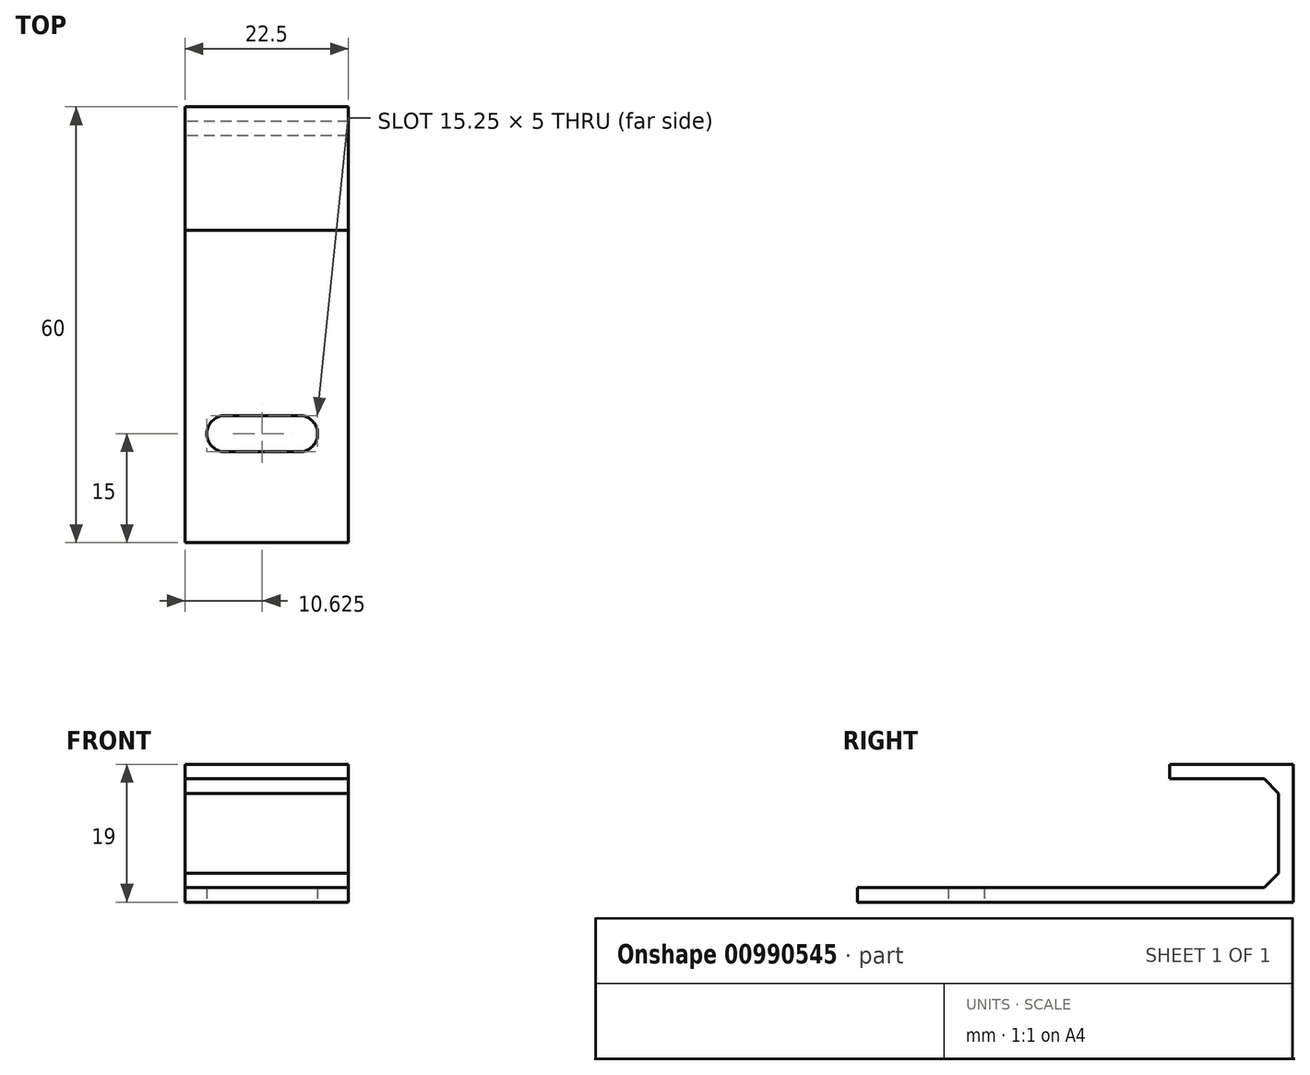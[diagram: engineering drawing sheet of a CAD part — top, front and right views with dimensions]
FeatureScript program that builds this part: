
annotation { "Feature Type Name" : "Feature", "Feature Type Description" : "" }
export const myFeature = defineFeature(function(context is Context, id is Id, definition is map)
    precondition{}
    {
        {
            assignVariable(context, id + "F0", {"name" : "noz", "anyValue" : .5});
        }
        {
            assignVariable(context, id + "F1", {"name" : "shells", "anyValue" : 4});
        }
        {
            assignVariable(context, id + "F2", {"name" : "wall", "anyValue" : getVariable(context, 'noz') * getVariable(context, 'shells')});
        }
        {
            assignVariable(context, id + "F3", {"name" : "hole", "anyValue" : 4.5});
        }
        {
            var Q0;
            Q0=qCreatedBy(makeId("Top.planeOp"),FACE);
            var sketch = newSketch(context, id + "F4", { "sketchPlane" : qUnion([Q0])});
            skLineSegment(sketch, "E0.bottom", {"start": v(21.25, 40.92) * mm, "end": v(-21.25, 40.92) * mm, "construction": true});
            skLineSegment(sketch, "E0.top", {"start": v(21.25, -40.93) * mm, "end": v(-21.25, -40.93) * mm, "construction": true});
            skLineSegment(sketch, "E0.left", {"start": v(21.25, 40.93) * mm, "end": v(21.25, -40.93) * mm, "construction": true});
            skLineSegment(sketch, "E0.right", {"start": v(-21.25, 40.93) * mm, "end": v(-21.25, -40.93) * mm, "construction": true});
            skPoint(sketch, "E0.middle", {"position": v(0, 0) * mm});
            skLineSegment(sketch, "E1.bottom", {"start": v(48, 75.25) * mm, "end": v(-48, 75.25) * mm, "construction": true});
            skLineSegment(sketch, "E1.top", {"start": v(48, -75.25) * mm, "end": v(-48, -75.25) * mm, "construction": true});
            skLineSegment(sketch, "E1.left", {"start": v(48, 75.25) * mm, "end": v(48, -75.25) * mm});
            skLineSegment(sketch, "E1.right", {"start": v(-48, 75.25) * mm, "end": v(-48, -75.25) * mm});
            skLineSegment(sketch, "E2.bottom", {"start": v(-6.25, 40.92) * mm, "end": v(6.25, 40.92) * mm, "construction": true});
            skLineSegment(sketch, "E2.top", {"start": v(-6.25, 45.92) * mm, "end": v(6.25, 45.92) * mm, "construction": true});
            skLineSegment(sketch, "E2.left", {"start": v(-6.25, 40.92) * mm, "end": v(-6.25, 45.92) * mm, "construction": true});
            skLineSegment(sketch, "E2.right", {"start": v(6.25, 40.92) * mm, "end": v(6.25, 45.92) * mm, "construction": true});
            skLineSegment(sketch, "E3.bottom", {"start": v(-21.25, 40.92) * mm, "end": v(-6.25, 40.92) * mm, "construction": true});
            skLineSegment(sketch, "E3.top", {"start": v(-21.25, 75.25) * mm, "end": v(-6.25, 75.25) * mm, "construction": true});
            skLineSegment(sketch, "E3.left", {"start": v(-21.25, 40.92) * mm, "end": v(-21.25, 75.25) * mm, "construction": true});
            skLineSegment(sketch, "E3.right", {"start": v(-6.25, 40.92) * mm, "end": v(-6.25, 75.25) * mm, "construction": true});
            skLineSegment(sketch, "E4.bottom", {"start": v(6.25, 40.92) * mm, "end": v(21.25, 40.92) * mm, "construction": true});
            skLineSegment(sketch, "E4.top", {"start": v(6.25, 75.25) * mm, "end": v(21.25, 75.25) * mm, "construction": true});
            skLineSegment(sketch, "E4.left", {"start": v(6.25, 40.92) * mm, "end": v(6.25, 75.25) * mm, "construction": true});
            skLineSegment(sketch, "E4.right", {"start": v(21.25, 40.92) * mm, "end": v(21.25, 75.25) * mm, "construction": true});
            skLineSegment(sketch, "E5", {"start": v(0, 91.05) * mm, "end": v(0, -104.71) * mm, "construction": true});
            skCircle(sketch, "E6", {"center": v(-43, 60.25) * mm, "radius": 2.5 * mm});
            skCircle(sketch, "E7.MirrorC", {"center": v(43, 60.25) * mm, "radius": 2.5 * mm});
            skLineSegment(sketch, "E8.bottom", {"start": v(-48, -75.25) * mm, "end": v(48, -75.25) * mm, "construction": true});
            skLineSegment(sketch, "E8.top", {"start": v(-48, -88.75) * mm, "end": v(48, -88.75) * mm, "construction": true});
            skLineSegment(sketch, "E8.left", {"start": v(-48, -75.25) * mm, "end": v(-48, -88.75) * mm, "construction": true});
            skLineSegment(sketch, "E8.right", {"start": v(48, -75.25) * mm, "end": v(48, -88.75) * mm, "construction": true});
            skCircle(sketch, "E9", {"center": v(0, -82) * mm, "radius": 2.5 * mm, "construction": true});
            skLineSegment(sketch, "E10.bottom", {"start": v(-48, 45.25) * mm, "end": v(48, 45.25) * mm});
            skLineSegment(sketch, "E10.top", {"start": v(-48, 105.25) * mm, "end": v(48, 105.25) * mm});
            skLineSegment(sketch, "E10.left", {"start": v(-48, 45.25) * mm, "end": v(-48, 105.25) * mm});
            skLineSegment(sketch, "E10.right", {"start": v(48, 45.25) * mm, "end": v(48, 105.25) * mm});
            skLineSegment(sketch, "E11", {"start": v(-48, 85.25) * mm, "end": v(48, 85.25) * mm});
            skLineSegment(sketch, "E12", {"start": v(-48, 103.25) * mm, "end": v(48, 103.25) * mm});
            skLineSegment(sketch, "E13", {"start": v(48, 60.25) * mm, "end": v(0, 60.25) * mm, "construction": true});
            skCircle(sketch, "E14", {"center": v(5.5, 60.25) * mm, "radius": 2.5 * mm});
            skLineSegment(sketch, "E15", {"start": v(22.5, 75.25) * mm, "end": v(22.5, 45.25) * mm, "construction": true});
            skCircle(sketch, "E16", {"center": v(15.75, 60.25) * mm, "radius": 2.5 * mm});
            skLineSegment(sketch, "E17", {"start": v(15.75, 57.75) * mm, "end": v(5.5, 57.75) * mm});
            skLineSegment(sketch, "E18", {"start": v(15.75, 62.75) * mm, "end": v(5.5, 62.75) * mm});
            skSolve(sketch);
        }
        {
            var Q0;
            Q0=qCreatedBy(makeId("Right.planeOp"),FACE);
            var sketch = newSketch(context, id + "F5", { "sketchPlane" : qUnion([Q0])});
            skLineSegment(sketch, "E19.0", {"start": v(45.25, 0) * mm, "end": v(105.25, 0) * mm});
            skLineSegment(sketch, "E20.0", {"start": v(62.75, 0) * mm, "end": v(57.75, 0) * mm});
            skPoint(sketch, "E21.0", {"position": v(85.25, 0) * mm});
            skPoint(sketch, "E22.0", {"position": v(103.25, 0) * mm});
            skLineSegment(sketch, "E23.top", {"start": v(45.25, 2) * mm, "end": v(103.25, 2) * mm});
            skLineSegment(sketch, "E23.left", {"start": v(45.25, 0) * mm, "end": v(45.25, 2) * mm});
            skLineSegment(sketch, "E23.right", {"start": v(105.25, 0) * mm, "end": v(105.25, 2) * mm});
            skLineSegment(sketch, "E24.left", {"start": v(103.25, 2) * mm, "end": v(103.25, 17) * mm});
            skLineSegment(sketch, "E24.right", {"start": v(105.25, -0.35) * mm, "end": v(105.25, 17) * mm});
            skLineSegment(sketch, "E25.bottom", {"start": v(103.25, 17) * mm, "end": v(88.25, 17) * mm});
            skLineSegment(sketch, "E25.top", {"start": v(105.25, 19) * mm, "end": v(88.25, 19) * mm});
            skLineSegment(sketch, "E25.left", {"start": v(105.25, 17) * mm, "end": v(105.25, 19) * mm});
            skLineSegment(sketch, "E25.right", {"start": v(88.25, 17) * mm, "end": v(88.25, 19) * mm});
            skSolve(sketch);
        }
        {
            var Q0;
            Q0 = qSketchRegion(id + "F5", true);
            extrude(context, id + "F6", {"entities" : qUnion([Q0]), "depth" : (getVariable(context, 'hole') * 5) * mm, "offsetDistance" : 25 * mm});
        }
        {
            var Q0;
            {var subQ0=sQuery(id+"F4.wireOp",EDGE,"E16");var subQ1=makeQuery(id+"F4.imprint","INTERSECT",VERTEX,{"derivedFrom":[subQ0,sQuery(id+"F4.wireOp",EDGE,"E17")]});Q0=makeQuery(id+"F4.imprint","IMPRINT",FACE,{"disambiguationData":[TD([[makeQuery(id+"F4.imprint","IMPRINT",EDGE,{"disambiguationData":[TD([[subQ1,1.0]])],"derivedFrom":subQ0}),1.0]])]});}
            var Q1;
            {var subQ0=sQuery(id+"F4.wireOp",EDGE,"E17");Q1=makeQuery(id+"F4.imprint","IMPRINT",FACE,{"disambiguationData":[TD([[makeQuery(id+"F4.imprint","IMPRINT",EDGE,{"derivedFrom":subQ0}),-1.0]])]});}
            var Q2;
            {var subQ0=sQuery(id+"F4.wireOp",EDGE,"E14");var subQ1=makeQuery(id+"F4.imprint","INTERSECT",VERTEX,{"derivedFrom":[subQ0,sQuery(id+"F4.wireOp",EDGE,"E17")]});Q2=makeQuery(id+"F4.imprint","IMPRINT",FACE,{"disambiguationData":[TD([[makeQuery(id+"F4.imprint","IMPRINT",EDGE,{"disambiguationData":[TD([[subQ1,1.0]])],"derivedFrom":subQ0}),1.0]])]});}
            extrude(context, id + "F7", {"entities" : qUnion([Q0, Q1, Q2]), "operationType" : NewBodyOperationType.REMOVE, "endBound" : BoundingType.UP_TO_NEXT, "depth" : 25 * mm, "offsetDistance" : 25 * mm});
        }
        {
            var Q0;
            Q0=makeQuery(id+"F6.opExtrude","SWEPT_EDGE",EDGE,{"disambiguationData":[OSD([sQuery(id+"F5.wireOp",EDGE,"E23.top"),sQuery(id+"F5.wireOp",EDGE,"E24.left")])]});
            var Q1;
            Q1=makeQuery(id+"F6.opExtrude","SWEPT_EDGE",EDGE,{"disambiguationData":[OSD([sQuery(id+"F5.wireOp",EDGE,"E24.left"),sQuery(id+"F5.wireOp",EDGE,"E25.bottom")])]});
            chamfer(context, id + "F8", {"entities" : qUnion([Q0, Q1]), "width" : (getVariable(context, 'wall')) * mm, "tangentPropagation" : true});
        }
    });
